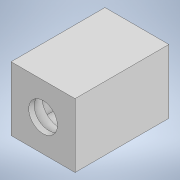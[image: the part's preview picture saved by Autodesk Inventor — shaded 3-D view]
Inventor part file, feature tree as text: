
AUTODESK INVENTOR PART (.ipt)
format: ipt  version: 2020.3 (Build 243373000, 373)  size: 126,976 bytes
history: native  units: mm
features: sketch x8, extrude x6
ambient origin geometry x8: Origin, YZ Plane, XZ Plane, XY Plane, X Axis, Y Axis, Z Axis, Center Point
bodies: Solid1 (feature_tree)
feature tree (14):
  extrude  "Extrusion1"  Depth=47.9mm
  extrude  "Extrusion2"  Depth=85.0mm TaperAngle=0.0deg
  extrude  "Extrusion3"  Depth=5.0mm
  sketch  "Sketch4"  dims[d8=8.0mm d9=0.0mm d10=10.0mm d11=0.0mm]
  extrude  "Extrusion4"  Depth=10.0mm TaperAngle=0.0deg
  sketch  "Sketch6"  dims[d15=26.0mm d16=5.0mm d17=0.0mm]
  extrude  "Extrusion5"  Depth=10.0mm TaperAngle=0.0deg
  extrude  "Extrusion6"  Depth=5.0mm TaperAngle=0.0deg
  sketch  "Sketch1"  dims[d0=47.9mm d1=47.9mm]
  sketch  "Sketch2"  dims[d2=5.0mm d3=85.0mm d4=0.0mm]
  sketch  "Sketch3"  dims[d5=5.0mm d6=0.0mm d7=32.0mm]
  sketch  "Sketch5"  dims[d12=32.0mm d13=10.0mm d14=0.0mm]
  sketch  "Sketch7"
  sketch  "Sketch8"
